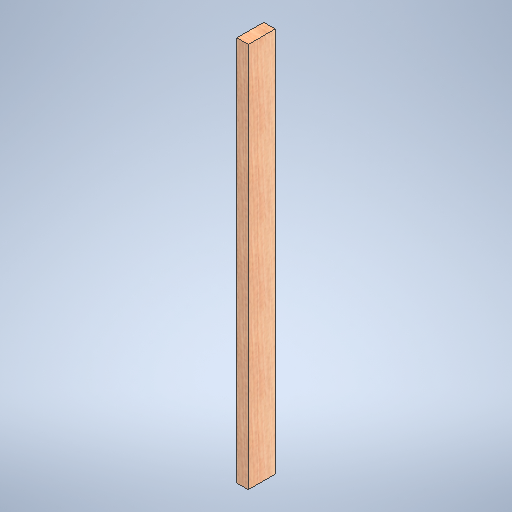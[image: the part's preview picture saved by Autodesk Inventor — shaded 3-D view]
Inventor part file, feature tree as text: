
AUTODESK INVENTOR PART (.ipt)
format: ipt  version: 2025 (Build 290162010, 162A)  size: 316,416 bytes
history: native  units: in
note: dims shown in document units (in); Inventor stores cm internally (conversion verified against a paired STEP export)
features: extrude x1, sketch x1
ambient origin geometry x8: Origin, YZ Plane, XZ Plane, XY Plane, X Axis, Y Axis, Z Axis, Center Point
bodies: Solid1 (feature_tree)
feature tree (2):
  extrude  "Extrusion1"  Depth=1.5in
  sketch  "Sketch1"  dims[d0=3.5in d1=1.5in d2=50.25in d3=0.0in]
